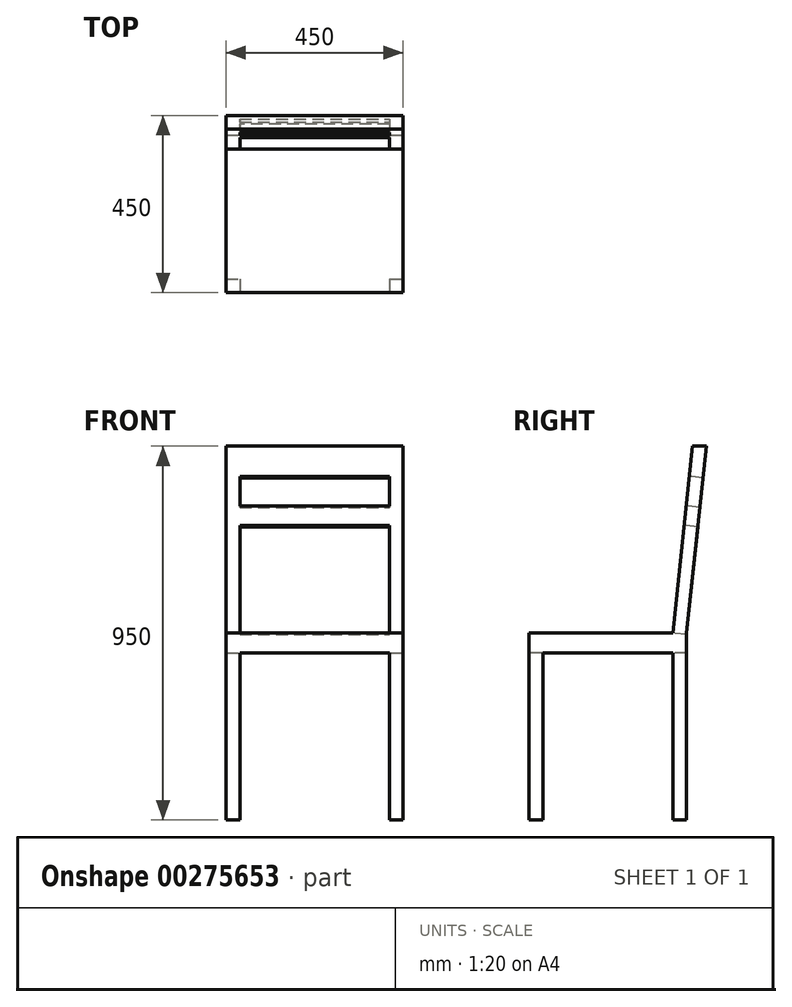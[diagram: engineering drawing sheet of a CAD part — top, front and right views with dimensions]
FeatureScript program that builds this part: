
annotation { "Feature Type Name" : "Feature", "Feature Type Description" : "" }
export const myFeature = defineFeature(function(context is Context, id is Id, definition is map)
    precondition{}
    {
        {
            var Q0;
            Q0=qCreatedBy(makeId("Top.planeOp"),FACE);
            var sketch = newSketch(context, id + "F0", { "sketchPlane" : qUnion([Q0])});
            skLineSegment(sketch, "E0.bottom", {"start": v(225, 225) * mm, "end": v(-225, 225) * mm});
            skLineSegment(sketch, "E0.top", {"start": v(225, -225) * mm, "end": v(-225, -225) * mm});
            skLineSegment(sketch, "E0.left", {"start": v(225, 225) * mm, "end": v(225, -225) * mm});
            skLineSegment(sketch, "E0.right", {"start": v(-225, 225) * mm, "end": v(-225, -225) * mm});
            skPoint(sketch, "E0.middle", {"position": v(0, 0) * mm});
            skSolve(sketch);
        }
        {
            var Q0;
            Q0=qSketchRegion(id+"F0",true);
            extrude(context, id + "F1", {"entities" : qUnion([Q0]), "depth" : 950 * mm});
        }
        {
            var Q0;
            Q0=makeQuery(id+"F1.opExtrude","SWEPT_FACE",FACE,{"disambiguationData":[OSD([sQuery(id+"F0.wireOp",EDGE,"E0.left")])]});
            var sketch = newSketch(context, id + "F2", { "sketchPlane" : qUnion([Q0])});
            skLineSegment(sketch, "E1.left", {"start": v(225, 475) * mm, "end": v(225, 473.04) * mm});
            skLineSegment(sketch, "E1.right", {"start": v(-225, 495.33) * mm, "end": v(-225, 493.37) * mm});
            skLineSegment(sketch, "E2.bottom", {"start": v(225, 475) * mm, "end": v(-225, 475) * mm});
            skLineSegment(sketch, "E2.top", {"start": v(225, 425) * mm, "end": v(-225, 425) * mm});
            skLineSegment(sketch, "E2.left", {"start": v(225, 475) * mm, "end": v(225, 425) * mm});
            skLineSegment(sketch, "E2.right", {"start": v(-225, 475) * mm, "end": v(-225, 425) * mm});
            skLineSegment(sketch, "E3", {"start": v(225, 950) * mm, "end": v(175, 475) * mm});
            skLineSegment(sketch, "E4", {"start": v(190, 950) * mm, "end": v(140, 475) * mm});
            skLineSegment(sketch, "E5", {"start": v(175, 475) * mm, "end": v(175, 0) * mm});
            skLineSegment(sketch, "E6", {"start": v(140, 425) * mm, "end": v(140, 0) * mm});
            skLineSegment(sketch, "E7", {"start": v(-190, 0) * mm, "end": v(-190, 425) * mm});
            skSolve(sketch);
        }
        {
            var Q0;
            {var subQ4=sQuery(id+"F2.wireOp",EDGE,"E5");var subQ6=sQuery(id+"F2.wireOp",EDGE,"E2.top");var subQ8=makeQuery(id+"F2.imprint","INTERSECT",VERTEX,{"derivedFrom":[subQ6,subQ4]});Q0=makeQuery(id+"F2.imprint","IMPRINT",FACE,{"disambiguationData":[TD([[makeQuery(id+"F2.imprint","IMPRINT",EDGE,{"disambiguationData":[TD([[subQ8,1.0]])],"derivedFrom":subQ4}),1.0]])]});}
            var Q1;
            {var subQ4=sQuery(id+"F2.wireOp",EDGE,"E1.right");Q1=makeQuery(id+"F2.imprint","IMPRINT",FACE,{"disambiguationData":[TD([[makeQuery(id+"F2.imprint","IMPRINT",EDGE,{"derivedFrom":subQ4}),1.0]])]});}
            var Q2;
            {var subQ0=sQuery(id+"F2.wireOp",EDGE,"E7");Q2=makeQuery(id+"F2.imprint","IMPRINT",FACE,{"disambiguationData":[TD([[makeQuery(id+"F2.imprint","IMPRINT",EDGE,{"derivedFrom":subQ0}),-1.0]])]});}
            var Q3;
            {var subQ1=sQuery(id+"F0.wireOp",EDGE,"E0.left");var subQ4=sQuery(id+"F2.wireOp",EDGE,"E5");var subQ6=makeQuery(id+"F1.opExtrude","CAP_EDGE",EDGE,{"disambiguationData":[OSD([subQ1])],"isStart":true});var subQ7=makeQuery(id+"F2.imprint","INTERSECT",VERTEX,{"derivedFrom":[subQ6,subQ4]});Q3=makeQuery(id+"F2.imprint","IMPRINT",FACE,{"disambiguationData":[TD([[makeQuery(id+"F2.imprint","IMPRINT",EDGE,{"disambiguationData":[TD([[subQ7,1.0]])],"derivedFrom":subQ4}),1.0]])]});}
            var Q4;
            {var subQ4=sQuery(id+"F2.wireOp",EDGE,"E3");Q4=makeQuery(id+"F2.imprint","IMPRINT",FACE,{"disambiguationData":[TD([[makeQuery(id+"F2.imprint","IMPRINT",EDGE,{"derivedFrom":subQ4}),1.0]])]});}
            extrude(context, id + "F3", {"entities" : qUnion([Q0, Q1, Q2, Q3, Q4]), "operationType" : NewBodyOperationType.REMOVE, "endBound" : BoundingType.THROUGH_ALL, "oppositeDirection" : true, "depth" : 25 * mm});
        }
        {
            var Q0;
            Q0=makeQuery(id+"F1.opExtrude","SWEPT_FACE",FACE,{"disambiguationData":[OSD([sQuery(id+"F0.wireOp",EDGE,"E0.top")])]});
            var sketch = newSketch(context, id + "F4", { "sketchPlane" : qUnion([Q0])});
            skLineSegment(sketch, "E8", {"start": v(-190, 0) * mm, "end": v(-190, 425) * mm});
            skLineSegment(sketch, "E9", {"start": v(-190, 425) * mm, "end": v(190, 425) * mm});
            skLineSegment(sketch, "E10", {"start": v(190, 425) * mm, "end": v(190, 0) * mm});
            skSolve(sketch);
        }
        {
            var Q0;
            Q0 = qSketchRegion(id + "F4", true);
            var Q1;
            {var subQ0=sQuery(id+"F4.wireOp",EDGE,"E8");Q1=makeQuery(id+"F4.imprint","IMPRINT",FACE,{"disambiguationData":[TD([[makeQuery(id+"F4.imprint","IMPRINT",EDGE,{"derivedFrom":subQ0}),-1.0]])]});}
            extrude(context, id + "F5", {"entities" : qUnion([Q0, Q1]), "operationType" : NewBodyOperationType.REMOVE, "endBound" : BoundingType.THROUGH_ALL, "oppositeDirection" : true, "depth" : 25 * mm});
        }
        {
            var Q0;
            Q0=makeQuery(id+"F3.boolean.opBoolean","COPY",FACE,{"derivedFrom":makeQuery(id+"F3.opExtrude","SWEPT_FACE",FACE,{"disambiguationData":[OSD([sQuery(id+"F2.wireOp",EDGE,"E4")])]})});
            var sketch = newSketch(context, id + "F6", { "sketchPlane" : qUnion([Q0])});
            skLineSegment(sketch, "E11", {"start": v(-190, 487.05) * mm, "end": v(-190, 887.05) * mm});
            skLineSegment(sketch, "E12", {"start": v(-190, 887.05) * mm, "end": v(190, 887.05) * mm});
            skLineSegment(sketch, "E13", {"start": v(190, 887.05) * mm, "end": v(190, 487.05) * mm});
            skLineSegment(sketch, "E14", {"start": v(-190, 812.05) * mm, "end": v(190, 812.05) * mm});
            skLineSegment(sketch, "E15", {"start": v(190, 762.05) * mm, "end": v(-190, 762.05) * mm});
            skSolve(sketch);
        }
        {
            var Q0;
            {var subQ0=sQuery(id+"F6.wireOp",EDGE,"E12");Q0=makeQuery(id+"F6.imprint","IMPRINT",FACE,{"disambiguationData":[TD([[makeQuery(id+"F6.imprint","IMPRINT",EDGE,{"derivedFrom":subQ0}),-1.0]])]});}
            var Q1;
            {var subQ3=sQuery(id+"F6.wireOp",EDGE,"E15");Q1=makeQuery(id+"F6.imprint","IMPRINT",FACE,{"disambiguationData":[TD([[makeQuery(id+"F6.imprint","IMPRINT",EDGE,{"derivedFrom":subQ3}),1.0]])]});}
            extrude(context, id + "F7", {"entities" : qUnion([Q0, Q1]), "operationType" : NewBodyOperationType.REMOVE, "endBound" : BoundingType.THROUGH_ALL, "oppositeDirection" : true, "depth" : 25 * mm});
        }
    });
